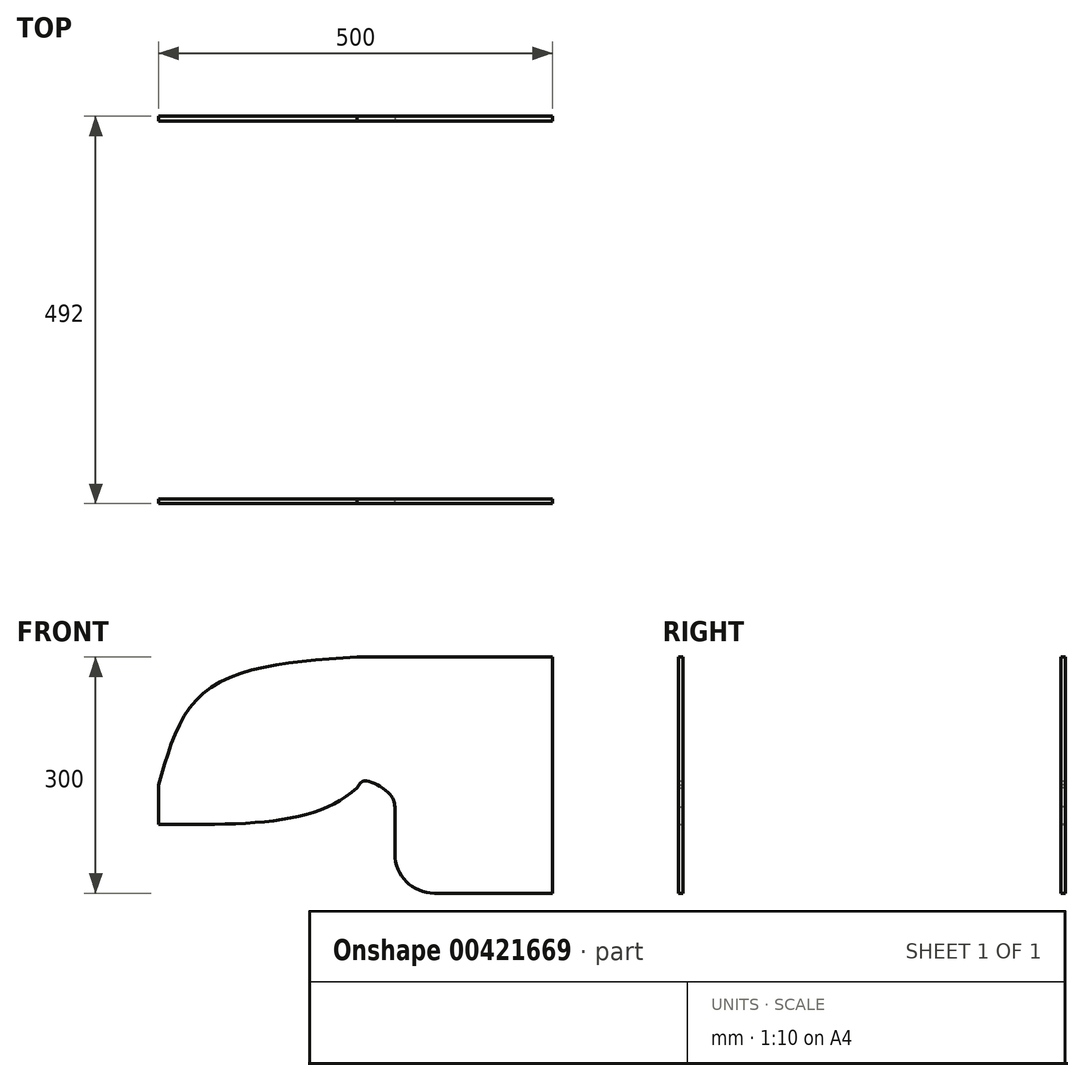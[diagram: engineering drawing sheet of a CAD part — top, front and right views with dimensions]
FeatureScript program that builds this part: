
annotation { "Feature Type Name" : "Feature", "Feature Type Description" : "" }
export const myFeature = defineFeature(function(context is Context, id is Id, definition is map)
    precondition{}
    {
        {
            var Q0;
            Q0=qCreatedBy(makeId("Front.planeOp"),FACE);
            cPlane(context, id + "F0", {"entities" : qUnion([Q0]), "cplaneType" : CPlaneType.OFFSET, "offset" : 240 * mm, "width" : 150 * mm, "height" : 150 * mm});
        }
        {
            var Q0;
            Q0=qCreatedBy(id+"F0.planeOp",FACE);
            var sketch = newSketch(context, id + "F1", { "sketchPlane" : qUnion([Q0])});
            skFitSpline(sketch, "E0", {"points": [v(-1521.03, 91.28) * mm, v(-1489.42, 125.65) * mm, v(-1238.54, 136.53) * mm, v(-1088, 181.73) * mm], "startDerivative": vector(-12.97, 259.48) * mm, "endDerivative": vector(291.65, 265.13) * mm});
            skLineSegment(sketch, "E1", {"start": v(-990, 48) * mm, "end": v(-840, 48) * mm});
            skLineSegment(sketch, "E2", {"start": v(-1340, 135.42) * mm, "end": v(-1340, 185.42) * mm});
            skLineSegment(sketch, "E3", {"start": v(-840, 48) * mm, "end": v(-840, 348) * mm});
            skLineSegment(sketch, "E4", {"start": v(-840, 348) * mm, "end": v(-1088, 348) * mm});
            skFitSpline(sketch, "E5", {"points": [v(-1340, 185.42) * mm, v(-1279.6, 305.16) * mm, v(-1088, 348) * mm], "startDerivative": vector(84.51, 306.78) * mm, "endDerivative": vector(409.2, 27.24) * mm});
            skLineSegment(sketch, "E6", {"start": v(-1040, 98) * mm, "end": v(-1040, 157.6) * mm});
            skFitSpline(sketch, "E7", {"points": [v(-1088, 181.73) * mm, v(-1079.1, 190.64) * mm, v(-1046.06, 173.3) * mm, v(-1040, 157.6) * mm], "startDerivative": vector(23.12, 48.65) * mm, "endDerivative": vector(5.5, -50.54) * mm});
            skPoint(sketch, "E8.visualSharp", {"position": v(-1040, 48) * mm});
            skArc(sketch, "E8.filletArc", {"start": v(-1040, 98) * mm, "mid": v(-1025.36, 62.64) * mm, "end": v(-990, 48) * mm});
            skSolve(sketch);
        }
        {
            var Q0;
            Q0=makeQuery(id+"F1.imprint","IMPRINT",FACE,{"disambiguationData":[TD([[makeQuery(id+"F1.imprint","IMPRINT",EDGE,{"derivedFrom":sQuery(id+"F1.wireOp",EDGE,"E0")}),1.0]])]});
            extrude(context, id + "F2", {"entities" : qUnion([Q0]), "depth" : 6 * mm});
        }
        {
            var Q0;
            Q0=makeQuery(id+"F2.opExtrude","SWEPT_BODY",BODY,{"disambiguationData":[OSD([sQuery(id+"F1.wireOp",EDGE,"E0"),sQuery(id+"F1.wireOp",EDGE,"E1"),sQuery(id+"F1.wireOp",EDGE,"E2"),sQuery(id+"F1.wireOp",EDGE,"E3"),sQuery(id+"F1.wireOp",EDGE,"E4"),sQuery(id+"F1.wireOp",EDGE,"E5"),sQuery(id+"F1.wireOp",EDGE,"E6"),sQuery(id+"F1.wireOp",EDGE,"310ad976-902e-4617-8676-227b50659fc2")])]});
            var Q1;
            Q1=qCreatedBy(makeId("Front.planeOp"),FACE);
            mirror(context, id + "F3", {"entities" : qUnion([Q0]), "mirrorPlane" : qUnion([Q1])});
        }
    });
